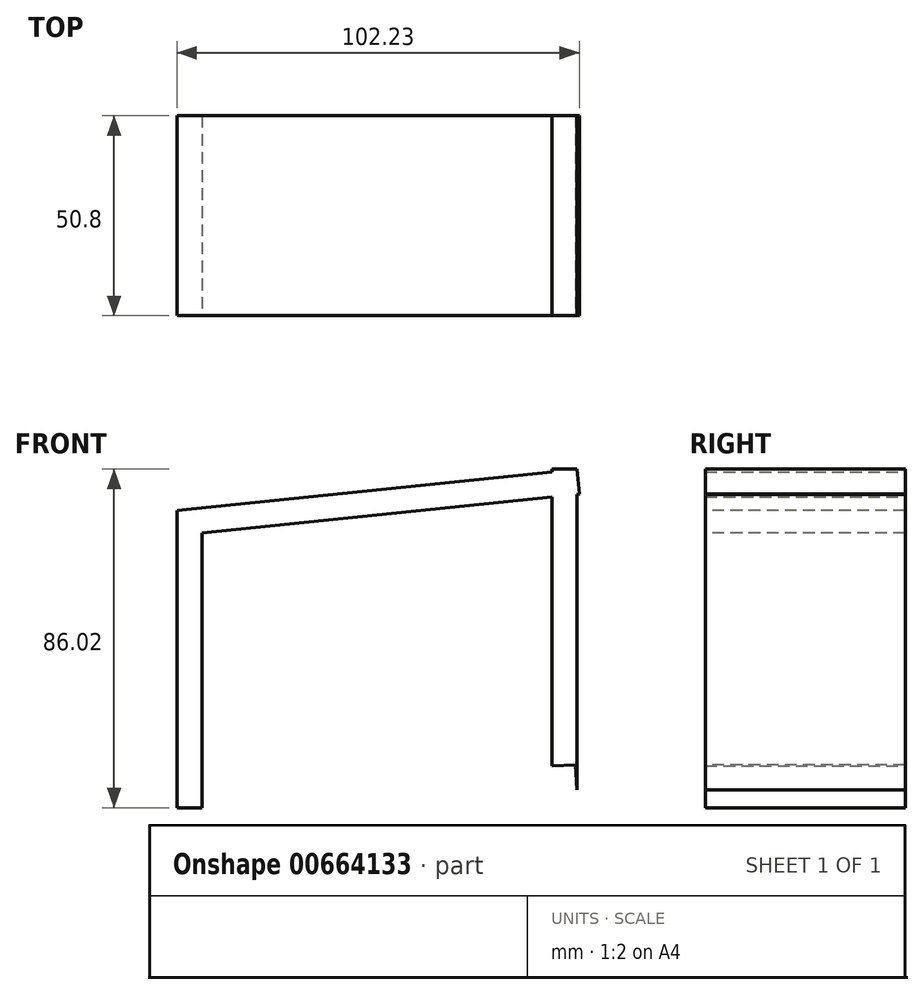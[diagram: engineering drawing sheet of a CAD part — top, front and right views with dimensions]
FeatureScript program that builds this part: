
annotation { "Feature Type Name" : "Feature", "Feature Type Description" : "" }
export const myFeature = defineFeature(function(context is Context, id is Id, definition is map)
    precondition{}
    {
        {
            var Q0;
            Q0=qCreatedBy(makeId("Front.planeOp"),FACE);
            var sketch = newSketch(context, id + "F0", { "sketchPlane" : qUnion([Q0])});
            skLineSegment(sketch, "E0", {"start": v(-59.8, 0) * mm, "end": v(-59.8, -75.59) * mm});
            skLineSegment(sketch, "E1", {"start": v(-59.8, -75.59) * mm, "end": v(41.77, -71) * mm});
            skLineSegment(sketch, "E2", {"start": v(41.77, -71) * mm, "end": v(41.77, 10.43) * mm});
            skLineSegment(sketch, "E3", {"start": v(-59.8, 0) * mm, "end": v(41.77, 10.43) * mm});
            skSolve(sketch);
        }
        {
            var Q0;
            Q0=sQuery(id+"F0.wireOp",EDGE,"E3");
            var Q1;
            Q1=sQuery(id+"F0.wireOp",EDGE,"E0");
            var Q2;
            Q2=sQuery(id+"F0.wireOp",EDGE,"E1");
            var Q3;
            Q3=sQuery(id+"F0.wireOp",EDGE,"E2");
            extrude(context, id + "F1", {"bodyType" : ToolBodyType.SURFACE, "surfaceEntities" : qUnion([Q0, Q1, Q2, Q3]), "depth" : 50.8 * mm, "offsetDistance" : 25.4 * mm});
        }
        {
            var Q0;
            Q0=makeQuery(id+"F1.opExtrude","SWEPT_FACE",FACE,{"disambiguationData":[OSD([sQuery(id+"F0.wireOp",EDGE,"E3")])]});
            extrude(context, id + "F2", {"entities" : qUnion([Q0]), "depth" : 6.35 * mm, "offsetDistance" : 25.4 * mm});
        }
        {
            var Q0;
            Q0=makeQuery(id+"F1.opExtrude","SWEPT_FACE",FACE,{"disambiguationData":[OSD([sQuery(id+"F0.wireOp",EDGE,"E2")])]});
            extrude(context, id + "F3", {"entities" : qUnion([Q0]), "operationType" : NewBodyOperationType.ADD, "depth" : 6.35 * mm, "offsetDistance" : 25.4 * mm});
        }
        {
            var Q0;
            Q0=makeQuery(id+"F1.opExtrude","SWEPT_FACE",FACE,{"disambiguationData":[OSD([sQuery(id+"F0.wireOp",EDGE,"E1")])]});
            var Q1;
            Q1=makeQuery(id+"F1.opExtrude","SWEPT_FACE",FACE,{"disambiguationData":[OSD([sQuery(id+"F0.wireOp",EDGE,"E0")])]});
            extrude(context, id + "F4", {"entities" : qUnion([Q0, Q1]), "operationType" : NewBodyOperationType.REMOVE, "depth" : 6.35 * mm, "offsetDistance" : 25.4 * mm});
        }
        {
            var Q0;
            Q0=makeQuery(id+"F1.opExtrude","SWEPT_FACE",FACE,{"disambiguationData":[OSD([sQuery(id+"F0.wireOp",EDGE,"E0")])]});
            extrude(context, id + "F5", {"entities" : qUnion([Q0]), "operationType" : NewBodyOperationType.ADD, "depth" : 6.35 * mm, "offsetDistance" : 25.4 * mm});
        }
    });
